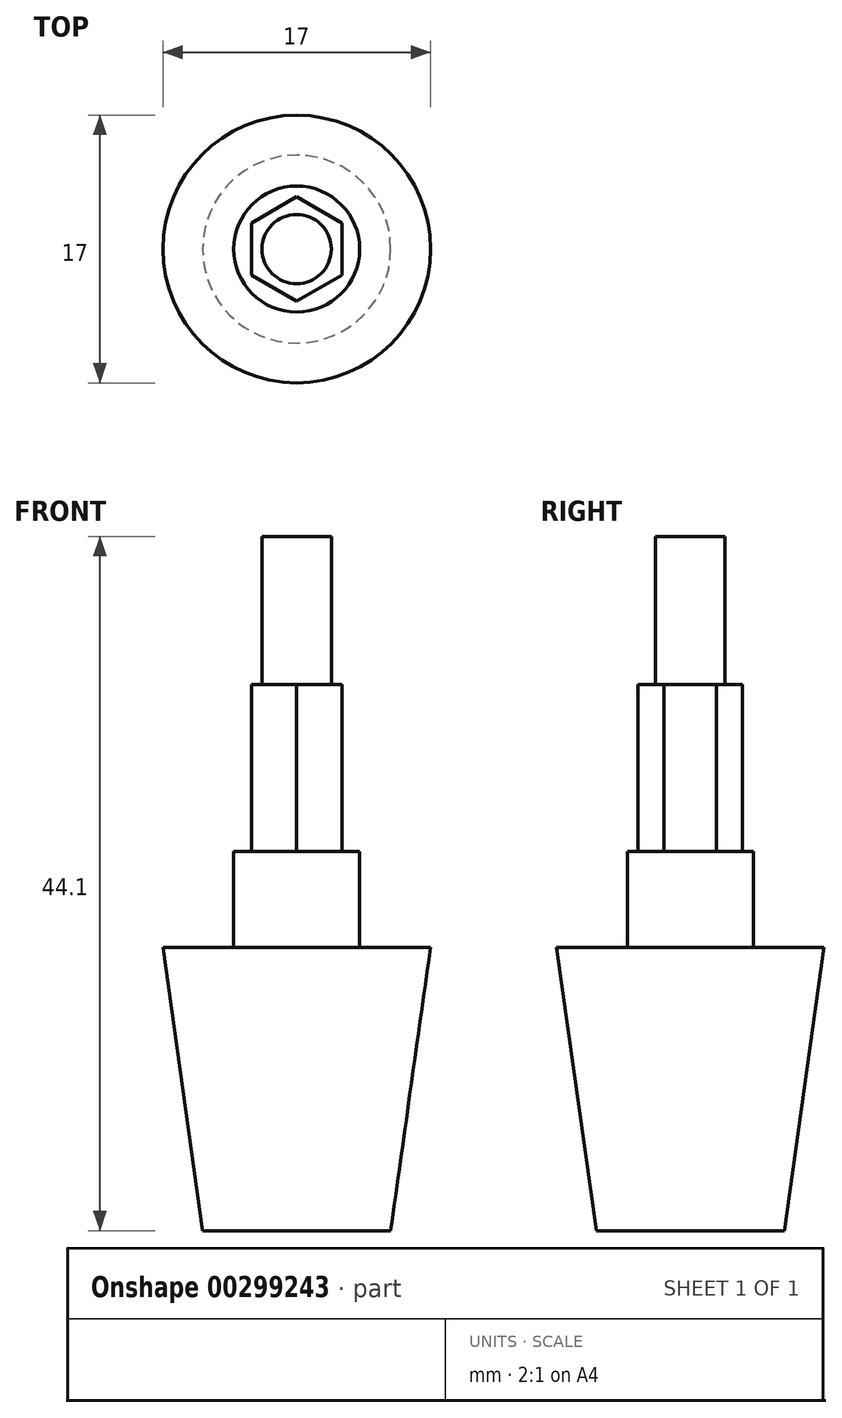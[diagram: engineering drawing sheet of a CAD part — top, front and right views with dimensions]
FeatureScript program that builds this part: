
annotation { "Feature Type Name" : "Feature", "Feature Type Description" : "" }
export const myFeature = defineFeature(function(context is Context, id is Id, definition is map)
    precondition{}
    {
        {
            var Q0;
            Q0=qCreatedBy(makeId("Top.planeOp"),FACE);
            var sketch = newSketch(context, id + "F0", { "sketchPlane" : qUnion([Q0])});
            skCircle(sketch, "E0", {"center": v(0, 0) * mm, "radius": 8.5 * mm});
            skSolve(sketch);
        }
        {
            var Q0;
            Q0=makeQuery(id+"F0.imprint","IMPRINT",FACE,{"disambiguationData":[TD([[makeQuery(id+"F0.imprint","IMPRINT",EDGE,{"derivedFrom":sQuery(id+"F0.wireOp",EDGE,"E0")}),1.0]])]});
            extrude(context, id + "F1", {"entities" : qUnion([Q0]), "oppositeDirection" : true, "depth" : 18 * mm, "hasDraft" : true, "draftAngle" : 8 * degree, "draftPullDirection" : true});
        }
        {
            var Q0;
            Q0=qCreatedBy(makeId("Top.planeOp"),FACE);
            var sketch = newSketch(context, id + "F2", { "sketchPlane" : qUnion([Q0])});
            skCircle(sketch, "E1", {"center": v(0, 0) * mm, "radius": 4 * mm});
            skSolve(sketch);
        }
        {
            var Q0;
            Q0=makeQuery(id+"F2.imprint","IMPRINT",FACE,{"disambiguationData":[TD([[makeQuery(id+"F2.imprint","IMPRINT",EDGE,{"derivedFrom":sQuery(id+"F2.wireOp",EDGE,"E1")}),1.0]])]});
            extrude(context, id + "F3", {"entities" : qUnion([Q0]), "operationType" : NewBodyOperationType.ADD, "depth" : 6.1 * mm});
        }
        {
            var Q0;
            Q0=makeQuery(id+"F3.opExtrude","CAP_FACE",FACE,{"disambiguationData":[OSD([sQuery(id+"F2.wireOp",EDGE,"E1")])],"isStart":false});
            var sketch = newSketch(context, id + "F4", { "sketchPlane" : qUnion([Q0])});
            skCircle(sketch, "E2.cCircle", {"center": v(0, 0) * mm, "radius": 2.87 * mm, "construction": true});
            skLineSegment(sketch, "E2.0", {"start": v(2.87, -1.66) * mm, "end": v(0, -3.31) * mm});
            skLineSegment(sketch, "E2.1", {"start": v(0, -3.31) * mm, "end": v(-2.87, -1.66) * mm});
            skLineSegment(sketch, "E2.2", {"start": v(-2.87, -1.66) * mm, "end": v(-2.87, 1.66) * mm});
            skLineSegment(sketch, "E2.3", {"start": v(-2.87, 1.66) * mm, "end": v(0, 3.31) * mm});
            skLineSegment(sketch, "E2.4", {"start": v(0, 3.31) * mm, "end": v(2.87, 1.66) * mm});
            skLineSegment(sketch, "E2.5", {"start": v(2.87, 1.66) * mm, "end": v(2.87, -1.66) * mm});
            skPoint(sketch, "E2.0.midPoint", {"position": v(1.43, -2.49) * mm});
            skSolve(sketch);
        }
        {
            var Q0;
            Q0=makeQuery(id+"F4.imprint","IMPRINT",FACE,{"disambiguationData":[TD([[makeQuery(id+"F4.imprint","IMPRINT",EDGE,{"derivedFrom":sQuery(id+"F4.wireOp",EDGE,"E2.0")}),-1.0]])]});
            extrude(context, id + "F5", {"entities" : qUnion([Q0]), "operationType" : NewBodyOperationType.ADD, "depth" : 10.6 * mm});
        }
        {
            var Q0;
            Q0=makeQuery(id+"F5.opExtrude","CAP_FACE",FACE,{"disambiguationData":[OSD([sQuery(id+"F4.wireOp",EDGE,"E2.0"),sQuery(id+"F4.wireOp",EDGE,"E2.1"),sQuery(id+"F4.wireOp",EDGE,"E2.2"),sQuery(id+"F4.wireOp",EDGE,"E2.3"),sQuery(id+"F4.wireOp",EDGE,"E2.4"),sQuery(id+"F4.wireOp",EDGE,"E2.5")])],"isStart":false});
            var sketch = newSketch(context, id + "F6", { "sketchPlane" : qUnion([Q0])});
            skCircle(sketch, "E3", {"center": v(0, 0) * mm, "radius": 2.2 * mm});
            skSolve(sketch);
        }
        {
            var Q0;
            Q0=makeQuery(id+"F6.imprint","IMPRINT",FACE,{"disambiguationData":[TD([[makeQuery(id+"F6.imprint","IMPRINT",EDGE,{"derivedFrom":sQuery(id+"F6.wireOp",EDGE,"E3")}),1.0]])]});
            extrude(context, id + "F7", {"entities" : qUnion([Q0]), "operationType" : NewBodyOperationType.ADD, "depth" : 9.4 * mm});
        }
    });
